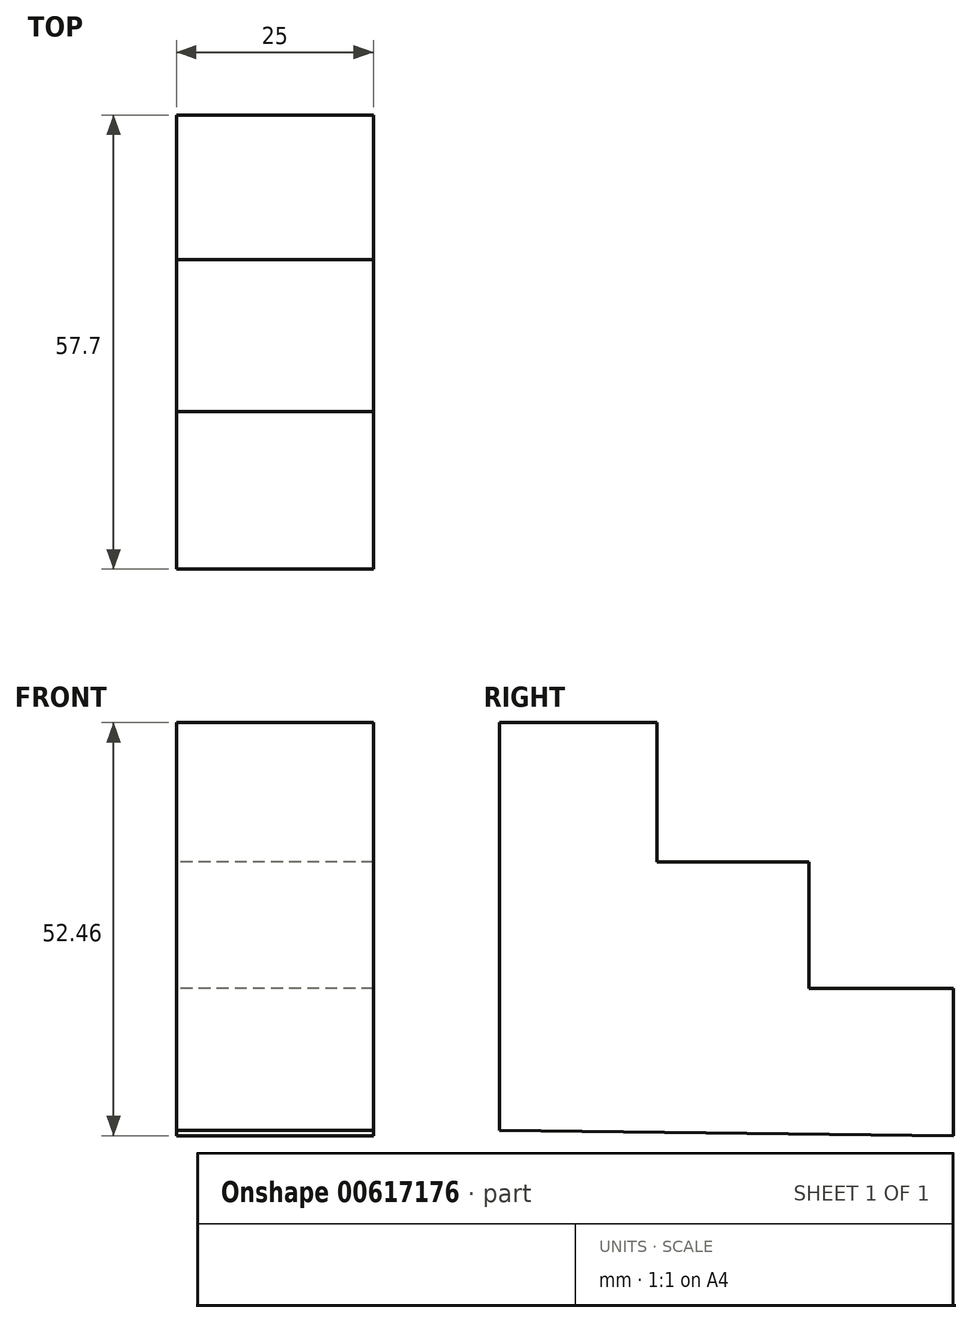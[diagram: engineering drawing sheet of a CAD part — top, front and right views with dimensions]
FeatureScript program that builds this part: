
annotation { "Feature Type Name" : "Feature", "Feature Type Description" : "" }
export const myFeature = defineFeature(function(context is Context, id is Id, definition is map)
    precondition{}
    {
        {
            var Q0;
            Q0=qCreatedBy(makeId("Right.planeOp"),FACE);
            var sketch = newSketch(context, id + "F0", { "sketchPlane" : qUnion([Q0])});
            skLineSegment(sketch, "E0", {"start": v(-61.4, 53.53) * mm, "end": v(-41.4, 53.53) * mm});
            skLineSegment(sketch, "E1", {"start": v(-41.4, 53.53) * mm, "end": v(-41.4, 35.82) * mm});
            skLineSegment(sketch, "E2", {"start": v(-41.4, 35.82) * mm, "end": v(-22.06, 35.82) * mm});
            skLineSegment(sketch, "E3", {"start": v(-22.06, 35.82) * mm, "end": v(-22.06, 19.76) * mm});
            skLineSegment(sketch, "E4", {"start": v(-22.06, 19.76) * mm, "end": v(-3.7, 19.76) * mm});
            skLineSegment(sketch, "E5", {"start": v(-3.7, 19.76) * mm, "end": v(-3.7, 1.07) * mm});
            skLineSegment(sketch, "E6", {"start": v(-61.4, 53.53) * mm, "end": v(-61.4, 1.73) * mm});
            skLineSegment(sketch, "E7", {"start": v(-61.4, 1.73) * mm, "end": v(-3.7, 1.07) * mm});
            skSolve(sketch);
        }
        {
            var Q0;
            Q0 = qSketchRegion(id + "F0", true);
            extrude(context, id + "F1", {"entities" : qUnion([Q0]), "depth" : 25 * mm, "offsetDistance" : 25 * mm});
        }
    });
